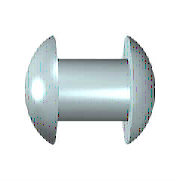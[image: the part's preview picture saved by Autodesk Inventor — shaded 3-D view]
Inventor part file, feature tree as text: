
AUTODESK INVENTOR PART (.ipt)
format: ipt  version: 2022 (Build 260153000, 153)  size: 160,768 bytes
history: native  units: mm (DEFAULTED — no unit token found)
features: sketch x1
ambient origin geometry x8: Origin, YZ Plane, XZ Plane, XY Plane, X Axis, Y Axis, Z Axis, Center Point
bodies: Solid1 (feature_tree), Body (feature_tree)
feature tree (1):
  sketch  "Sketch"  dims[d0=12.7mm d1=0.0264mm d2=20.32mm d3=8.89mm d4=20.32mm d5=8.89mm d11=90.0deg d7=0.0mm d15=0.0mm d16=0.0mm]
